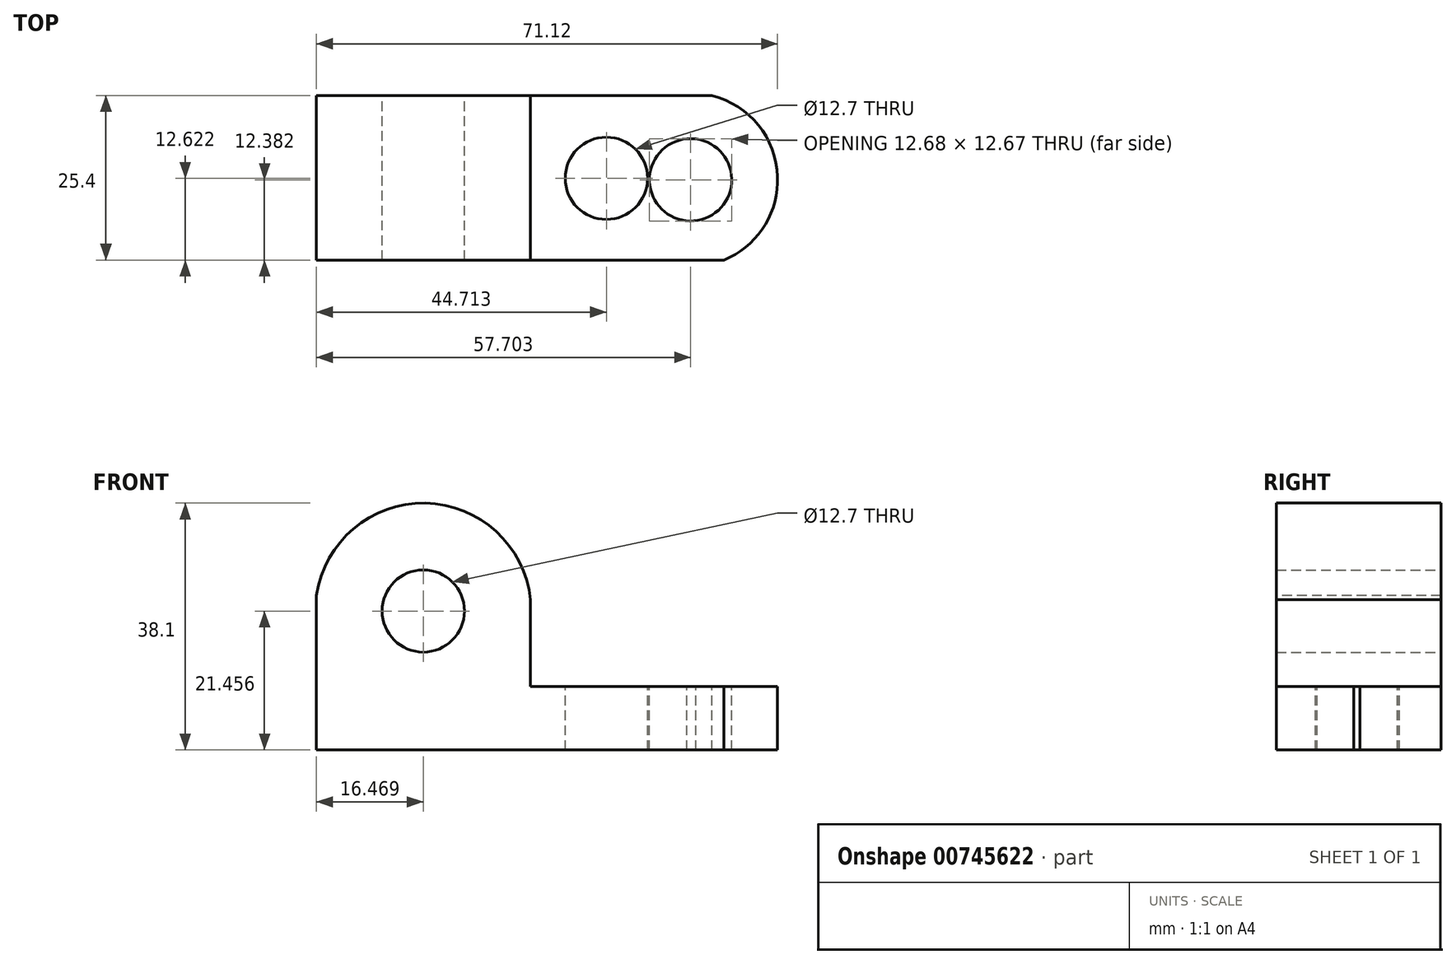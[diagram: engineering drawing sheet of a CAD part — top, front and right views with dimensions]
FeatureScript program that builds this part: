
annotation { "Feature Type Name" : "Feature", "Feature Type Description" : "" }
export const myFeature = defineFeature(function(context is Context, id is Id, definition is map)
    precondition{}
    {
        {
            var Q0;
            Q0=qCreatedBy(makeId("Front.planeOp"),FACE);
            var sketch = newSketch(context, id + "F0", { "sketchPlane" : qUnion([Q0])});
            skLineSegment(sketch, "E0", {"start": v(0, 0) * mm, "end": v(71.12, 0) * mm});
            skLineSegment(sketch, "E1", {"start": v(71.12, 0) * mm, "end": v(71.12, 9.78) * mm});
            skLineSegment(sketch, "E2", {"start": v(71.12, 9.78) * mm, "end": v(33.02, 9.78) * mm});
            skLineSegment(sketch, "E3", {"start": v(33.02, 9.78) * mm, "end": v(33.02, 38.1) * mm});
            skLineSegment(sketch, "E4", {"start": v(33.02, 38.1) * mm, "end": v(0, 38.1) * mm});
            skLineSegment(sketch, "E5", {"start": v(0, 38.1) * mm, "end": v(0, 0) * mm});
            skSolve(sketch);
        }
        {
            var Q0;
            Q0=makeQuery(id+"F0.imprint","IMPRINT",FACE,{"disambiguationData":[TD([[makeQuery(id+"F0.imprint","IMPRINT",EDGE,{"derivedFrom":sQuery(id+"F0.wireOp",EDGE,"E0")}),1.0]])]});
            extrude(context, id + "F1", {"entities" : qUnion([Q0]), "depth" : 25.4 * mm, "offsetDistance" : 25.4 * mm});
        }
        {
            var Q0;
            Q0=makeQuery(id+"F1.opExtrude","CAP_FACE",FACE,{"disambiguationData":[OSD([sQuery(id+"F0.wireOp",EDGE,"E0"),sQuery(id+"F0.wireOp",EDGE,"E1"),sQuery(id+"F0.wireOp",EDGE,"E2"),sQuery(id+"F0.wireOp",EDGE,"E3"),sQuery(id+"F0.wireOp",EDGE,"E4"),sQuery(id+"F0.wireOp",EDGE,"E5")])],"isStart":false});
            var sketch = newSketch(context, id + "F2", { "sketchPlane" : qUnion([Q0])});
            skArc(sketch, "E6", {"start": v(33.02, 19.7) * mm, "mid": v(16.14, 38.1) * mm, "end": v(0, 19.05) * mm});
            skSolve(sketch);
        }
        {
            var Q0;
            {var subQ5=makeQuery(id+"F1.opExtrude","CAP_EDGE",EDGE,{"disambiguationData":[OSD([sQuery(id+"F0.wireOp",EDGE,"E4")])],"isStart":false});Q0=makeQuery(id+"F2.imprint","IMPRINT",FACE,{"disambiguationData":[TD([[makeQuery(id+"F2.imprint","IMPRINT",EDGE,{"derivedFrom":subQ5}),1.0]])]});}
            extrude(context, id + "F3", {"entities" : qUnion([Q0]), "operationType" : NewBodyOperationType.REMOVE, "endBound" : BoundingType.THROUGH_ALL, "oppositeDirection" : true, "depth" : 25.4 * mm, "offsetDistance" : 25.4 * mm});
        }
        {
            var Q0;
            Q0=makeQuery(id+"F1.opExtrude","SWEPT_FACE",FACE,{"disambiguationData":[OSD([sQuery(id+"F0.wireOp",EDGE,"E2")])]});
            var sketch = newSketch(context, id + "F4", { "sketchPlane" : qUnion([Q0])});
            skArc(sketch, "E7", {"start": v(62.85, -25.4) * mm, "mid": v(71.1, -12.04) * mm, "end": v(61.02, 0) * mm});
            skSolve(sketch);
        }
        {
            var Q0;
            {var subQ0=sQuery(id+"F4.wireOp",EDGE,"E7");var subQ1=sQuery(id+"F0.wireOp",EDGE,"E2");var subQ2=makeQuery(id+"F1.opExtrude","CAP_EDGE",EDGE,{"disambiguationData":[OSD([subQ1])],"isStart":true});var subQ3=makeQuery(id+"F4.imprint","INTERSECT",VERTEX,{"derivedFrom":[subQ2,subQ0]});Q0=makeQuery(id+"F4.imprint","IMPRINT",FACE,{"disambiguationData":[TD([[makeQuery(id+"F4.imprint","IMPRINT",EDGE,{"disambiguationData":[TD([[subQ3,1.0]])],"derivedFrom":subQ0}),-1.0]])]});}
            var Q1;
            {var subQ0=sQuery(id+"F4.wireOp",EDGE,"E7");var subQ1=sQuery(id+"F0.wireOp",EDGE,"E2");var subQ2=makeQuery(id+"F1.opExtrude","CAP_EDGE",EDGE,{"disambiguationData":[OSD([subQ1])],"isStart":false});var subQ3=makeQuery(id+"F4.imprint","INTERSECT",VERTEX,{"derivedFrom":[subQ2,subQ0]});Q1=makeQuery(id+"F4.imprint","IMPRINT",FACE,{"disambiguationData":[TD([[makeQuery(id+"F4.imprint","IMPRINT",EDGE,{"disambiguationData":[TD([[subQ3,-1.0]])],"derivedFrom":subQ0}),-1.0]])]});}
            extrude(context, id + "F5", {"entities" : qUnion([Q0, Q1]), "operationType" : NewBodyOperationType.REMOVE, "endBound" : BoundingType.THROUGH_ALL, "oppositeDirection" : true, "depth" : 25.4 * mm, "offsetDistance" : 25.4 * mm});
        }
        {
            var Q0;
            Q0=makeQuery(id+"F1.opExtrude","CAP_FACE",FACE,{"disambiguationData":[OSD([sQuery(id+"F0.wireOp",EDGE,"E0"),sQuery(id+"F0.wireOp",EDGE,"E1"),sQuery(id+"F0.wireOp",EDGE,"E2"),sQuery(id+"F0.wireOp",EDGE,"E3"),sQuery(id+"F0.wireOp",EDGE,"E4"),sQuery(id+"F0.wireOp",EDGE,"E5")])],"isStart":true});
            var sketch = newSketch(context, id + "F6", { "sketchPlane" : qUnion([Q0])});
            skCircle(sketch, "E8", {"center": v(-16.47, 21.46) * mm, "radius": 6.35 * mm});
            skSolve(sketch);
        }
        {
            var Q0;
            Q0=makeQuery(id+"F6.imprint","IMPRINT",FACE,{"disambiguationData":[TD([[makeQuery(id+"F6.imprint","IMPRINT",EDGE,{"derivedFrom":sQuery(id+"F6.wireOp",EDGE,"E8")}),1.0]])]});
            extrude(context, id + "F7", {"entities" : qUnion([Q0]), "operationType" : NewBodyOperationType.REMOVE, "endBound" : BoundingType.THROUGH_ALL, "oppositeDirection" : true, "depth" : 25.4 * mm, "offsetDistance" : 25.4 * mm});
        }
        {
            var Q0;
            Q0=makeQuery(id+"F1.opExtrude","SWEPT_FACE",FACE,{"disambiguationData":[OSD([sQuery(id+"F0.wireOp",EDGE,"E2")])]});
            var sketch = newSketch(context, id + "F8", { "sketchPlane" : qUnion([Q0])});
            skCircle(sketch, "E9", {"center": v(57.7, -13) * mm, "radius": 6.35 * mm});
            skCircle(sketch, "E10", {"center": v(44.71, -12.78) * mm, "radius": 6.35 * mm});
            skSolve(sketch);
        }
        {
            var Q0;
            Q0=makeQuery(id+"F8.imprint","IMPRINT",FACE,{"disambiguationData":[TD([[makeQuery(id+"F8.imprint","IMPRINT",EDGE,{"derivedFrom":sQuery(id+"F8.wireOp",EDGE,"E9")}),-1.0]])]});
            var sketch = newSketch(context, id + "F9", { "sketchPlane" : qUnion([Q0])});
            skLineSegment(sketch, "E11", {"start": v(44.04, -19.12) * mm, "end": v(58, -19.36) * mm});
            skSolve(sketch);
        }
        {
            var Q0;
            Q0=makeQuery(id+"F8.imprint","IMPRINT",FACE,{"disambiguationData":[TD([[makeQuery(id+"F8.imprint","IMPRINT",EDGE,{"derivedFrom":sQuery(id+"F8.wireOp",EDGE,"E9")}),-1.0]])]});
            var sketch = newSketch(context, id + "F10", { "sketchPlane" : qUnion([Q0])});
            skLineSegment(sketch, "E12", {"start": v(44.17, -6.44) * mm, "end": v(58.79, -6.71) * mm});
            skSolve(sketch);
        }
        {
            var Q0;
            {var subQ0=sQuery(id+"F10.wireOp",EDGE,"E12");var subQ1=makeQuery(id+"F8.imprint","IMPRINT",EDGE,{"derivedFrom":sQuery(id+"F8.wireOp",EDGE,"E9")});var subQ2=makeQuery(id+"F10.imprint","INTERSECT",VERTEX,{"disambiguationData":[OD(0.0)],"derivedFrom":[subQ1,subQ0]});Q0=makeQuery(id+"F10.imprint","IMPRINT",FACE,{"disambiguationData":[TD([[makeQuery(id+"F10.imprint","IMPRINT",EDGE,{"disambiguationData":[TD([[subQ2,-1.0]])],"derivedFrom":subQ0}),-1.0]])]});}
            var Q1;
            Q1=makeQuery(id+"F8.imprint","IMPRINT",FACE,{"disambiguationData":[TD([[makeQuery(id+"F8.imprint","IMPRINT",EDGE,{"derivedFrom":sQuery(id+"F8.wireOp",EDGE,"E10")}),1.0]])]});
            extrude(context, id + "F11", {"entities" : qUnion([Q0, Q1]), "operationType" : NewBodyOperationType.REMOVE, "endBound" : BoundingType.THROUGH_ALL, "oppositeDirection" : true, "depth" : 25.4 * mm, "offsetDistance" : 25.4 * mm});
        }
    });
